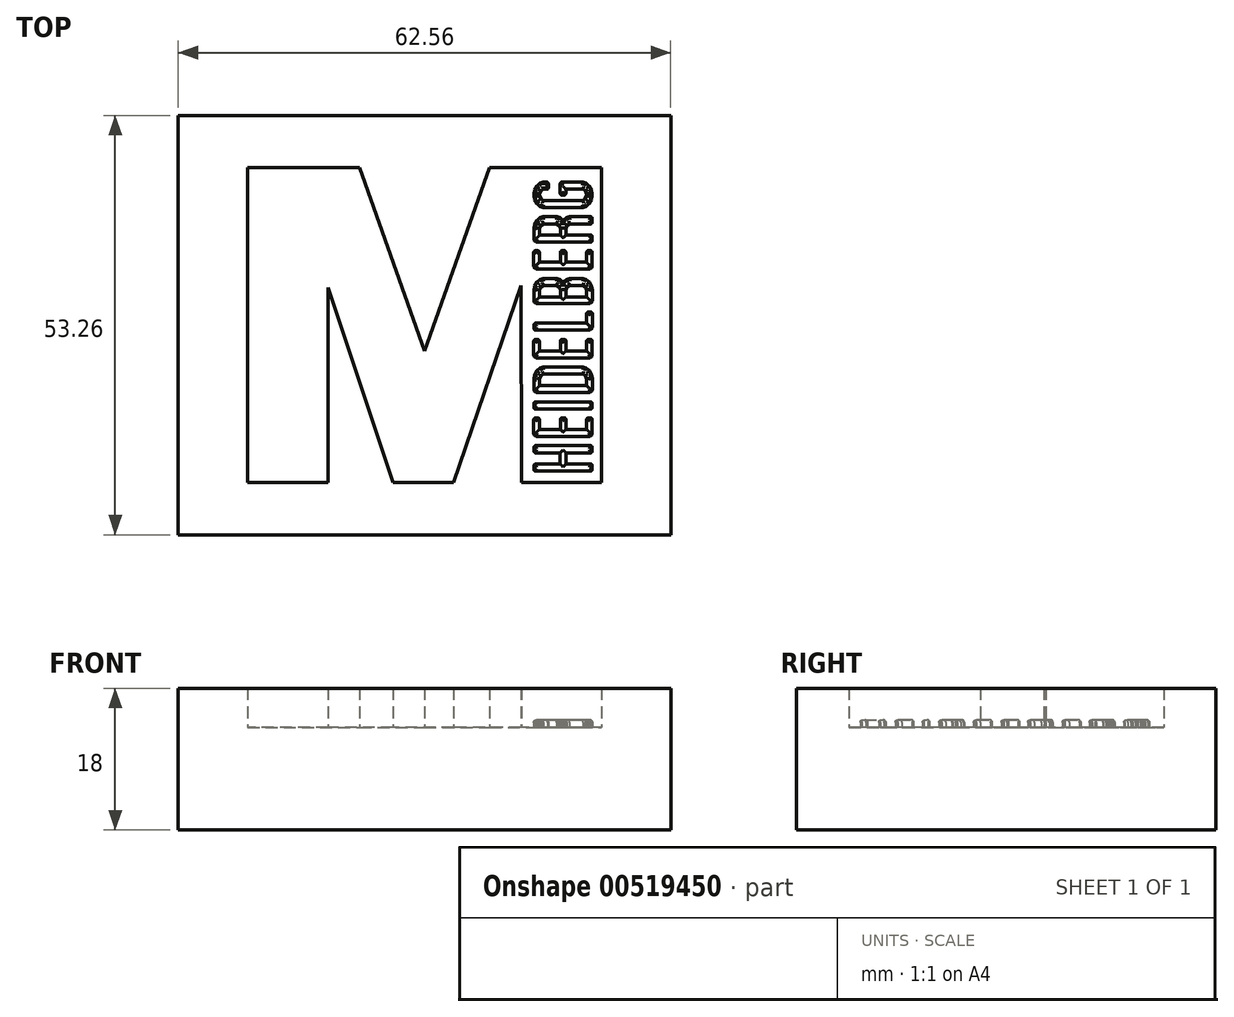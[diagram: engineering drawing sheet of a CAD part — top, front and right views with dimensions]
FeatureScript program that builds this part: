
annotation { "Feature Type Name" : "Feature", "Feature Type Description" : "" }
export const myFeature = defineFeature(function(context is Context, id is Id, definition is map)
    precondition{}
    {
        {
            var Q0;
            Q0=qCreatedBy(makeId("Top.planeOp"),FACE);
            var sketch = newSketch(context, id + "F0", { "sketchPlane" : qUnion([Q0])});
            skLineSegment(sketch, "E0", {"start": v(-22.46, 20) * mm, "end": v(-8.25, 20) * mm});
            skLineSegment(sketch, "E1", {"start": v(-8.25, 20) * mm, "end": v(0, -3.3) * mm});
            skLineSegment(sketch, "E2", {"start": v(0, -3.3) * mm, "end": v(8.3, 20) * mm});
            skLineSegment(sketch, "E3", {"start": v(8.3, 20) * mm, "end": v(22.46, 20) * mm});
            skLineSegment(sketch, "E4", {"start": v(22.46, 20) * mm, "end": v(22.46, -19.99) * mm});
            skLineSegment(sketch, "E5", {"start": v(22.46, -19.99) * mm, "end": v(12.3, -19.99) * mm});
            skLineSegment(sketch, "E6", {"start": v(12.3, -19.99) * mm, "end": v(12.26, 5.06) * mm});
            skLineSegment(sketch, "E7", {"start": v(12.26, 5.06) * mm, "end": v(3.69, -19.99) * mm});
            skLineSegment(sketch, "E8", {"start": v(3.69, -19.99) * mm, "end": v(-4.01, -19.99) * mm});
            skLineSegment(sketch, "E9", {"start": v(-4.01, -19.99) * mm, "end": v(-12.26, 4.79) * mm});
            skLineSegment(sketch, "E10", {"start": v(-12.26, 4.79) * mm, "end": v(-12.26, -20) * mm});
            skLineSegment(sketch, "E11", {"start": v(-12.26, -20) * mm, "end": v(-22.46, -20) * mm});
            skLineSegment(sketch, "E12", {"start": v(-22.46, -20) * mm, "end": v(-22.46, 20) * mm});
            skLineSegment(sketch, "E13", {"start": v(14.09, -15.3) * mm, "end": v(21.13, -15.3) * mm});
            skLineSegment(sketch, "E14", {"start": v(21.13, -15.3) * mm, "end": v(21.16, -15.3) * mm});
            skLineSegment(sketch, "E15", {"start": v(21.16, -15.3) * mm, "end": v(21.25, -15.37) * mm});
            skLineSegment(sketch, "E16", {"start": v(21.25, -15.37) * mm, "end": v(21.3, -15.5) * mm});
            skLineSegment(sketch, "E17", {"start": v(21.3, -15.5) * mm, "end": v(21.3, -15.54) * mm});
            skLineSegment(sketch, "E18", {"start": v(21.3, -15.54) * mm, "end": v(21.3, -15.98) * mm});
            skLineSegment(sketch, "E19", {"start": v(21.3, -15.98) * mm, "end": v(21.3, -16.02) * mm});
            skLineSegment(sketch, "E20", {"start": v(21.3, -16.02) * mm, "end": v(21.25, -16.14) * mm});
            skLineSegment(sketch, "E21", {"start": v(21.25, -16.14) * mm, "end": v(21.16, -16.2) * mm});
            skLineSegment(sketch, "E22", {"start": v(21.16, -16.2) * mm, "end": v(21.13, -16.2) * mm});
            skLineSegment(sketch, "E23", {"start": v(21.13, -16.2) * mm, "end": v(17.97, -16.2) * mm});
            skLineSegment(sketch, "E24", {"start": v(17.97, -16.2) * mm, "end": v(17.97, -17.65) * mm});
            skLineSegment(sketch, "E25", {"start": v(17.97, -17.65) * mm, "end": v(21.13, -17.65) * mm});
            skLineSegment(sketch, "E26", {"start": v(21.13, -17.65) * mm, "end": v(21.16, -17.65) * mm});
            skLineSegment(sketch, "E27", {"start": v(21.16, -17.65) * mm, "end": v(21.25, -17.71) * mm});
            skLineSegment(sketch, "E28", {"start": v(21.25, -17.71) * mm, "end": v(21.3, -17.84) * mm});
            skLineSegment(sketch, "E29", {"start": v(21.3, -17.84) * mm, "end": v(21.3, -17.88) * mm});
            skLineSegment(sketch, "E30", {"start": v(21.3, -17.88) * mm, "end": v(21.3, -18.32) * mm});
            skLineSegment(sketch, "E31", {"start": v(21.3, -18.32) * mm, "end": v(21.3, -18.36) * mm});
            skLineSegment(sketch, "E32", {"start": v(21.3, -18.36) * mm, "end": v(21.25, -18.49) * mm});
            skLineSegment(sketch, "E33", {"start": v(21.25, -18.49) * mm, "end": v(21.16, -18.55) * mm});
            skLineSegment(sketch, "E34", {"start": v(21.16, -18.55) * mm, "end": v(21.13, -18.55) * mm});
            skLineSegment(sketch, "E35", {"start": v(21.13, -18.55) * mm, "end": v(14.07, -18.55) * mm});
            skLineSegment(sketch, "E36", {"start": v(14.07, -18.55) * mm, "end": v(14.04, -18.55) * mm});
            skLineSegment(sketch, "E37", {"start": v(14.04, -18.55) * mm, "end": v(13.95, -18.49) * mm});
            skLineSegment(sketch, "E38", {"start": v(13.95, -18.49) * mm, "end": v(13.9, -18.36) * mm});
            skLineSegment(sketch, "E39", {"start": v(13.9, -18.36) * mm, "end": v(13.9, -18.32) * mm});
            skLineSegment(sketch, "E40", {"start": v(13.9, -18.32) * mm, "end": v(13.9, -17.88) * mm});
            skLineSegment(sketch, "E41", {"start": v(13.9, -17.88) * mm, "end": v(13.9, -17.84) * mm});
            skLineSegment(sketch, "E42", {"start": v(13.9, -17.84) * mm, "end": v(13.95, -17.71) * mm});
            skLineSegment(sketch, "E43", {"start": v(13.95, -17.71) * mm, "end": v(14.04, -17.65) * mm});
            skLineSegment(sketch, "E44", {"start": v(14.04, -17.65) * mm, "end": v(14.07, -17.65) * mm});
            skLineSegment(sketch, "E45", {"start": v(14.07, -17.65) * mm, "end": v(17.24, -17.65) * mm});
            skLineSegment(sketch, "E46", {"start": v(17.24, -17.65) * mm, "end": v(17.24, -16.2) * mm});
            skLineSegment(sketch, "E47", {"start": v(17.24, -16.2) * mm, "end": v(14.07, -16.2) * mm});
            skLineSegment(sketch, "E48", {"start": v(14.07, -16.2) * mm, "end": v(14.04, -16.2) * mm});
            skLineSegment(sketch, "E49", {"start": v(14.04, -16.2) * mm, "end": v(13.95, -16.14) * mm});
            skLineSegment(sketch, "E50", {"start": v(13.95, -16.14) * mm, "end": v(13.9, -16.02) * mm});
            skLineSegment(sketch, "E51", {"start": v(13.9, -16.02) * mm, "end": v(13.9, -15.98) * mm});
            skLineSegment(sketch, "E52", {"start": v(13.9, -15.98) * mm, "end": v(13.9, -15.54) * mm});
            skLineSegment(sketch, "E53", {"start": v(13.9, -15.54) * mm, "end": v(13.9, -15.5) * mm});
            skLineSegment(sketch, "E54", {"start": v(13.9, -15.5) * mm, "end": v(14.04, -15.3) * mm});
            skLineSegment(sketch, "E55", {"start": v(14.04, -15.3) * mm, "end": v(14.09, -15.3) * mm});
            skLineSegment(sketch, "E56", {"start": v(14.63, -13.23) * mm, "end": v(17.26, -13.23) * mm});
            skLineSegment(sketch, "E57", {"start": v(17.26, -13.23) * mm, "end": v(17.26, -12) * mm});
            skLineSegment(sketch, "E58", {"start": v(17.26, -12) * mm, "end": v(17.26, -11.96) * mm});
            skLineSegment(sketch, "E59", {"start": v(17.26, -11.96) * mm, "end": v(17.3, -11.84) * mm});
            skLineSegment(sketch, "E60", {"start": v(17.3, -11.84) * mm, "end": v(17.4, -11.78) * mm});
            skLineSegment(sketch, "E61", {"start": v(17.4, -11.78) * mm, "end": v(17.43, -11.78) * mm});
            skLineSegment(sketch, "E62", {"start": v(17.43, -11.78) * mm, "end": v(17.8, -11.78) * mm});
            skLineSegment(sketch, "E63", {"start": v(17.8, -11.78) * mm, "end": v(17.82, -11.78) * mm});
            skLineSegment(sketch, "E64", {"start": v(17.82, -11.78) * mm, "end": v(17.91, -11.84) * mm});
            skLineSegment(sketch, "E65", {"start": v(17.91, -11.84) * mm, "end": v(17.97, -11.96) * mm});
            skLineSegment(sketch, "E66", {"start": v(17.97, -11.96) * mm, "end": v(17.97, -12) * mm});
            skLineSegment(sketch, "E67", {"start": v(17.97, -12) * mm, "end": v(17.97, -13.23) * mm});
            skLineSegment(sketch, "E68", {"start": v(17.97, -13.23) * mm, "end": v(20.6, -13.23) * mm});
            skLineSegment(sketch, "E69", {"start": v(20.6, -13.23) * mm, "end": v(20.6, -12) * mm});
            skLineSegment(sketch, "E70", {"start": v(20.6, -12) * mm, "end": v(20.6, -11.96) * mm});
            skLineSegment(sketch, "E71", {"start": v(20.6, -11.96) * mm, "end": v(20.65, -11.84) * mm});
            skLineSegment(sketch, "E72", {"start": v(20.65, -11.84) * mm, "end": v(20.74, -11.78) * mm});
            skLineSegment(sketch, "E73", {"start": v(20.74, -11.78) * mm, "end": v(20.77, -11.78) * mm});
            skLineSegment(sketch, "E74", {"start": v(20.77, -11.78) * mm, "end": v(21.13, -11.78) * mm});
            skLineSegment(sketch, "E75", {"start": v(21.13, -11.78) * mm, "end": v(21.16, -11.78) * mm});
            skLineSegment(sketch, "E76", {"start": v(21.16, -11.78) * mm, "end": v(21.25, -11.84) * mm});
            skLineSegment(sketch, "E77", {"start": v(21.25, -11.84) * mm, "end": v(21.3, -11.96) * mm});
            skLineSegment(sketch, "E78", {"start": v(21.3, -11.96) * mm, "end": v(21.3, -12) * mm});
            skLineSegment(sketch, "E79", {"start": v(21.3, -12) * mm, "end": v(21.3, -13.67) * mm});
            skLineSegment(sketch, "E80", {"start": v(21.3, -13.67) * mm, "end": v(21.3, -13.75) * mm});
            skLineSegment(sketch, "E81", {"start": v(21.3, -13.75) * mm, "end": v(21.2, -13.99) * mm});
            skLineSegment(sketch, "E82", {"start": v(21.2, -13.99) * mm, "end": v(21, -14.12) * mm});
            skLineSegment(sketch, "E83", {"start": v(21, -14.12) * mm, "end": v(20.94, -14.12) * mm});
            skLineSegment(sketch, "E84", {"start": v(20.94, -14.12) * mm, "end": v(14.24, -14.12) * mm});
            skLineSegment(sketch, "E85", {"start": v(14.24, -14.12) * mm, "end": v(14.18, -14.12) * mm});
            skLineSegment(sketch, "E86", {"start": v(14.18, -14.12) * mm, "end": v(13.99, -13.99) * mm});
            skLineSegment(sketch, "E87", {"start": v(13.99, -13.99) * mm, "end": v(13.88, -13.75) * mm});
            skLineSegment(sketch, "E88", {"start": v(13.88, -13.75) * mm, "end": v(13.88, -13.67) * mm});
            skLineSegment(sketch, "E89", {"start": v(13.88, -13.67) * mm, "end": v(13.88, -12) * mm});
            skLineSegment(sketch, "E90", {"start": v(13.88, -12) * mm, "end": v(13.88, -11.96) * mm});
            skLineSegment(sketch, "E91", {"start": v(13.88, -11.96) * mm, "end": v(13.93, -11.84) * mm});
            skLineSegment(sketch, "E92", {"start": v(13.93, -11.84) * mm, "end": v(14.02, -11.78) * mm});
            skLineSegment(sketch, "E93", {"start": v(14.02, -11.78) * mm, "end": v(14.05, -11.78) * mm});
            skLineSegment(sketch, "E94", {"start": v(14.05, -11.78) * mm, "end": v(14.41, -11.78) * mm});
            skLineSegment(sketch, "E95", {"start": v(14.41, -11.78) * mm, "end": v(14.44, -11.78) * mm});
            skLineSegment(sketch, "E96", {"start": v(14.44, -11.78) * mm, "end": v(14.54, -11.84) * mm});
            skLineSegment(sketch, "E97", {"start": v(14.54, -11.84) * mm, "end": v(14.59, -11.96) * mm});
            skLineSegment(sketch, "E98", {"start": v(14.59, -11.96) * mm, "end": v(14.59, -12) * mm});
            skLineSegment(sketch, "E99", {"start": v(14.59, -12) * mm, "end": v(14.59, -13.23) * mm});
            skLineSegment(sketch, "E100", {"start": v(14.59, -13.23) * mm, "end": v(14.63, -13.23) * mm});
            skLineSegment(sketch, "E101", {"start": v(21.13, -9.74) * mm, "end": v(21.16, -9.74) * mm});
            skLineSegment(sketch, "E102", {"start": v(21.16, -9.74) * mm, "end": v(21.25, -9.8) * mm});
            skLineSegment(sketch, "E103", {"start": v(21.25, -9.8) * mm, "end": v(21.3, -9.93) * mm});
            skLineSegment(sketch, "E104", {"start": v(21.3, -9.93) * mm, "end": v(21.3, -9.97) * mm});
            skLineSegment(sketch, "E105", {"start": v(21.3, -9.97) * mm, "end": v(21.3, -10.41) * mm});
            skLineSegment(sketch, "E106", {"start": v(21.3, -10.41) * mm, "end": v(21.3, -10.45) * mm});
            skLineSegment(sketch, "E107", {"start": v(21.3, -10.45) * mm, "end": v(21.25, -10.58) * mm});
            skLineSegment(sketch, "E108", {"start": v(21.25, -10.58) * mm, "end": v(21.16, -10.64) * mm});
            skLineSegment(sketch, "E109", {"start": v(21.16, -10.64) * mm, "end": v(21.13, -10.64) * mm});
            skLineSegment(sketch, "E110", {"start": v(21.13, -10.64) * mm, "end": v(14.07, -10.64) * mm});
            skLineSegment(sketch, "E111", {"start": v(14.07, -10.64) * mm, "end": v(14.04, -10.64) * mm});
            skLineSegment(sketch, "E112", {"start": v(14.04, -10.64) * mm, "end": v(13.95, -10.58) * mm});
            skLineSegment(sketch, "E113", {"start": v(13.95, -10.58) * mm, "end": v(13.9, -10.45) * mm});
            skLineSegment(sketch, "E114", {"start": v(13.9, -10.45) * mm, "end": v(13.9, -10.41) * mm});
            skLineSegment(sketch, "E115", {"start": v(13.9, -10.41) * mm, "end": v(13.9, -9.97) * mm});
            skLineSegment(sketch, "E116", {"start": v(13.9, -9.97) * mm, "end": v(13.9, -9.93) * mm});
            skLineSegment(sketch, "E117", {"start": v(13.9, -9.93) * mm, "end": v(13.95, -9.8) * mm});
            skLineSegment(sketch, "E118", {"start": v(13.95, -9.8) * mm, "end": v(14.04, -9.74) * mm});
            skLineSegment(sketch, "E119", {"start": v(14.04, -9.74) * mm, "end": v(14.07, -9.74) * mm});
            skLineSegment(sketch, "E120", {"start": v(14.07, -9.74) * mm, "end": v(21.13, -9.74) * mm});
            skLineSegment(sketch, "E121", {"start": v(15.2, -5.33) * mm, "end": v(20.04, -5.33) * mm});
            skLineSegment(sketch, "E122", {"start": v(20.04, -5.33) * mm, "end": v(20.16, -5.33) * mm});
            skLineSegment(sketch, "E123", {"start": v(20.16, -5.33) * mm, "end": v(20.54, -5.45) * mm});
            skLineSegment(sketch, "E124", {"start": v(20.54, -5.45) * mm, "end": v(20.95, -5.8) * mm});
            skLineSegment(sketch, "E125", {"start": v(20.95, -5.8) * mm, "end": v(21.22, -6.3) * mm});
            skLineSegment(sketch, "E126", {"start": v(21.22, -6.3) * mm, "end": v(21.32, -6.78) * mm});
            skLineSegment(sketch, "E127", {"start": v(21.32, -6.78) * mm, "end": v(21.32, -6.94) * mm});
            skLineSegment(sketch, "E128", {"start": v(21.32, -6.94) * mm, "end": v(21.32, -8.1) * mm});
            skLineSegment(sketch, "E129", {"start": v(21.32, -8.1) * mm, "end": v(21.32, -8.18) * mm});
            skLineSegment(sketch, "E130", {"start": v(21.32, -8.18) * mm, "end": v(21.22, -8.42) * mm});
            skLineSegment(sketch, "E131", {"start": v(21.22, -8.42) * mm, "end": v(21.02, -8.55) * mm});
            skLineSegment(sketch, "E132", {"start": v(21.02, -8.55) * mm, "end": v(20.96, -8.55) * mm});
            skLineSegment(sketch, "E133", {"start": v(20.96, -8.55) * mm, "end": v(14.26, -8.55) * mm});
            skLineSegment(sketch, "E134", {"start": v(14.26, -8.55) * mm, "end": v(14.2, -8.55) * mm});
            skLineSegment(sketch, "E135", {"start": v(14.2, -8.55) * mm, "end": v(14, -8.42) * mm});
            skLineSegment(sketch, "E136", {"start": v(14, -8.42) * mm, "end": v(13.9, -8.18) * mm});
            skLineSegment(sketch, "E137", {"start": v(13.9, -8.18) * mm, "end": v(13.9, -8.1) * mm});
            skLineSegment(sketch, "E138", {"start": v(13.9, -8.1) * mm, "end": v(13.9, -6.94) * mm});
            skLineSegment(sketch, "E139", {"start": v(13.9, -6.94) * mm, "end": v(13.9, -6.78) * mm});
            skLineSegment(sketch, "E140", {"start": v(13.9, -6.78) * mm, "end": v(14, -6.3) * mm});
            skLineSegment(sketch, "E141", {"start": v(14, -6.3) * mm, "end": v(14.29, -5.8) * mm});
            skLineSegment(sketch, "E142", {"start": v(14.29, -5.8) * mm, "end": v(14.7, -5.45) * mm});
            skLineSegment(sketch, "E143", {"start": v(14.7, -5.45) * mm, "end": v(15.08, -5.33) * mm});
            skLineSegment(sketch, "E144", {"start": v(15.08, -5.33) * mm, "end": v(15.2, -5.33) * mm});
            skLineSegment(sketch, "E145", {"start": v(15.2, -6.23) * mm, "end": v(15.1, -6.23) * mm});
            skLineSegment(sketch, "E146", {"start": v(15.1, -6.23) * mm, "end": v(14.8, -6.44) * mm});
            skLineSegment(sketch, "E147", {"start": v(14.8, -6.44) * mm, "end": v(14.63, -6.81) * mm});
            skLineSegment(sketch, "E148", {"start": v(14.63, -6.81) * mm, "end": v(14.63, -6.94) * mm});
            skLineSegment(sketch, "E149", {"start": v(14.63, -6.94) * mm, "end": v(14.63, -7.67) * mm});
            skLineSegment(sketch, "E150", {"start": v(14.63, -7.67) * mm, "end": v(20.6, -7.67) * mm});
            skLineSegment(sketch, "E151", {"start": v(20.6, -7.67) * mm, "end": v(20.6, -6.94) * mm});
            skLineSegment(sketch, "E152", {"start": v(20.6, -6.94) * mm, "end": v(20.6, -6.81) * mm});
            skLineSegment(sketch, "E153", {"start": v(20.6, -6.81) * mm, "end": v(20.43, -6.44) * mm});
            skLineSegment(sketch, "E154", {"start": v(20.43, -6.44) * mm, "end": v(20.12, -6.23) * mm});
            skLineSegment(sketch, "E155", {"start": v(20.12, -6.23) * mm, "end": v(20.02, -6.23) * mm});
            skLineSegment(sketch, "E156", {"start": v(20.02, -6.23) * mm, "end": v(15.2, -6.23) * mm});
            skLineSegment(sketch, "E157", {"start": v(14.63, -3.27) * mm, "end": v(17.26, -3.27) * mm});
            skLineSegment(sketch, "E158", {"start": v(17.26, -3.27) * mm, "end": v(17.26, -2.04) * mm});
            skLineSegment(sketch, "E159", {"start": v(17.26, -2.04) * mm, "end": v(17.26, -2) * mm});
            skLineSegment(sketch, "E160", {"start": v(17.26, -2) * mm, "end": v(17.3, -1.88) * mm});
            skLineSegment(sketch, "E161", {"start": v(17.3, -1.88) * mm, "end": v(17.4, -1.81) * mm});
            skLineSegment(sketch, "E162", {"start": v(17.4, -1.81) * mm, "end": v(17.43, -1.81) * mm});
            skLineSegment(sketch, "E163", {"start": v(17.43, -1.81) * mm, "end": v(17.8, -1.81) * mm});
            skLineSegment(sketch, "E164", {"start": v(17.8, -1.81) * mm, "end": v(17.82, -1.81) * mm});
            skLineSegment(sketch, "E165", {"start": v(17.82, -1.81) * mm, "end": v(17.91, -1.88) * mm});
            skLineSegment(sketch, "E166", {"start": v(17.91, -1.88) * mm, "end": v(17.97, -2) * mm});
            skLineSegment(sketch, "E167", {"start": v(17.97, -2) * mm, "end": v(17.97, -2.04) * mm});
            skLineSegment(sketch, "E168", {"start": v(17.97, -2.04) * mm, "end": v(17.97, -3.27) * mm});
            skLineSegment(sketch, "E169", {"start": v(17.97, -3.27) * mm, "end": v(20.6, -3.27) * mm});
            skLineSegment(sketch, "E170", {"start": v(20.6, -3.27) * mm, "end": v(20.6, -2.04) * mm});
            skLineSegment(sketch, "E171", {"start": v(20.6, -2.04) * mm, "end": v(20.6, -2) * mm});
            skLineSegment(sketch, "E172", {"start": v(20.6, -2) * mm, "end": v(20.65, -1.88) * mm});
            skLineSegment(sketch, "E173", {"start": v(20.65, -1.88) * mm, "end": v(20.74, -1.81) * mm});
            skLineSegment(sketch, "E174", {"start": v(20.74, -1.81) * mm, "end": v(20.77, -1.81) * mm});
            skLineSegment(sketch, "E175", {"start": v(20.77, -1.81) * mm, "end": v(21.13, -1.81) * mm});
            skLineSegment(sketch, "E176", {"start": v(21.13, -1.81) * mm, "end": v(21.16, -1.81) * mm});
            skLineSegment(sketch, "E177", {"start": v(21.16, -1.81) * mm, "end": v(21.25, -1.88) * mm});
            skLineSegment(sketch, "E178", {"start": v(21.25, -1.88) * mm, "end": v(21.3, -2) * mm});
            skLineSegment(sketch, "E179", {"start": v(21.3, -2) * mm, "end": v(21.3, -2.04) * mm});
            skLineSegment(sketch, "E180", {"start": v(21.3, -2.04) * mm, "end": v(21.3, -3.71) * mm});
            skLineSegment(sketch, "E181", {"start": v(21.3, -3.71) * mm, "end": v(21.3, -3.8) * mm});
            skLineSegment(sketch, "E182", {"start": v(21.3, -3.8) * mm, "end": v(21.2, -4.03) * mm});
            skLineSegment(sketch, "E183", {"start": v(21.2, -4.03) * mm, "end": v(21, -4.16) * mm});
            skLineSegment(sketch, "E184", {"start": v(21, -4.16) * mm, "end": v(20.94, -4.16) * mm});
            skLineSegment(sketch, "E185", {"start": v(20.94, -4.16) * mm, "end": v(14.24, -4.16) * mm});
            skLineSegment(sketch, "E186", {"start": v(14.24, -4.16) * mm, "end": v(14.18, -4.16) * mm});
            skLineSegment(sketch, "E187", {"start": v(14.18, -4.16) * mm, "end": v(13.99, -4.03) * mm});
            skLineSegment(sketch, "E188", {"start": v(13.99, -4.03) * mm, "end": v(13.88, -3.8) * mm});
            skLineSegment(sketch, "E189", {"start": v(13.88, -3.8) * mm, "end": v(13.88, -3.71) * mm});
            skLineSegment(sketch, "E190", {"start": v(13.88, -3.71) * mm, "end": v(13.88, -2.04) * mm});
            skLineSegment(sketch, "E191", {"start": v(13.88, -2.04) * mm, "end": v(13.88, -2) * mm});
            skLineSegment(sketch, "E192", {"start": v(13.88, -2) * mm, "end": v(13.93, -1.88) * mm});
            skLineSegment(sketch, "E193", {"start": v(13.93, -1.88) * mm, "end": v(14.02, -1.81) * mm});
            skLineSegment(sketch, "E194", {"start": v(14.02, -1.81) * mm, "end": v(14.05, -1.81) * mm});
            skLineSegment(sketch, "E195", {"start": v(14.05, -1.81) * mm, "end": v(14.41, -1.81) * mm});
            skLineSegment(sketch, "E196", {"start": v(14.41, -1.81) * mm, "end": v(14.44, -1.81) * mm});
            skLineSegment(sketch, "E197", {"start": v(14.44, -1.81) * mm, "end": v(14.54, -1.88) * mm});
            skLineSegment(sketch, "E198", {"start": v(14.54, -1.88) * mm, "end": v(14.59, -2) * mm});
            skLineSegment(sketch, "E199", {"start": v(14.59, -2) * mm, "end": v(14.59, -2.04) * mm});
            skLineSegment(sketch, "E200", {"start": v(14.59, -2.04) * mm, "end": v(14.59, -3.27) * mm});
            skLineSegment(sketch, "E201", {"start": v(14.59, -3.27) * mm, "end": v(14.63, -3.27) * mm});
            skLineSegment(sketch, "E202", {"start": v(20.79, 1.68) * mm, "end": v(21.15, 1.68) * mm});
            skLineSegment(sketch, "E203", {"start": v(21.15, 1.68) * mm, "end": v(21.18, 1.68) * mm});
            skLineSegment(sketch, "E204", {"start": v(21.18, 1.68) * mm, "end": v(21.27, 1.62) * mm});
            skLineSegment(sketch, "E205", {"start": v(21.27, 1.62) * mm, "end": v(21.32, 1.5) * mm});
            skLineSegment(sketch, "E206", {"start": v(21.32, 1.5) * mm, "end": v(21.32, 1.45) * mm});
            skLineSegment(sketch, "E207", {"start": v(21.32, 1.45) * mm, "end": v(21.32, -0.2) * mm});
            skLineSegment(sketch, "E208", {"start": v(21.32, -0.2) * mm, "end": v(21.32, -0.28) * mm});
            skLineSegment(sketch, "E209", {"start": v(21.32, -0.28) * mm, "end": v(21.22, -0.51) * mm});
            skLineSegment(sketch, "E210", {"start": v(21.22, -0.51) * mm, "end": v(21.02, -0.64) * mm});
            skLineSegment(sketch, "E211", {"start": v(21.02, -0.64) * mm, "end": v(20.96, -0.64) * mm});
            skLineSegment(sketch, "E212", {"start": v(20.96, -0.64) * mm, "end": v(14.09, -0.64) * mm});
            skLineSegment(sketch, "E213", {"start": v(14.09, -0.64) * mm, "end": v(14.06, -0.64) * mm});
            skLineSegment(sketch, "E214", {"start": v(14.06, -0.64) * mm, "end": v(13.97, -0.58) * mm});
            skLineSegment(sketch, "E215", {"start": v(13.97, -0.58) * mm, "end": v(13.92, -0.45) * mm});
            skLineSegment(sketch, "E216", {"start": v(13.92, -0.45) * mm, "end": v(13.92, -0.41) * mm});
            skLineSegment(sketch, "E217", {"start": v(13.92, -0.41) * mm, "end": v(13.92, 0.03) * mm});
            skLineSegment(sketch, "E218", {"start": v(13.92, 0.03) * mm, "end": v(13.92, 0.07) * mm});
            skLineSegment(sketch, "E219", {"start": v(13.92, 0.07) * mm, "end": v(13.97, 0.19) * mm});
            skLineSegment(sketch, "E220", {"start": v(13.97, 0.19) * mm, "end": v(14.06, 0.26) * mm});
            skLineSegment(sketch, "E221", {"start": v(14.06, 0.26) * mm, "end": v(14.09, 0.26) * mm});
            skLineSegment(sketch, "E222", {"start": v(14.09, 0.26) * mm, "end": v(20.6, 0.26) * mm});
            skLineSegment(sketch, "E223", {"start": v(20.6, 0.26) * mm, "end": v(20.6, 1.47) * mm});
            skLineSegment(sketch, "E224", {"start": v(20.6, 1.47) * mm, "end": v(20.6, 1.5) * mm});
            skLineSegment(sketch, "E225", {"start": v(20.6, 1.5) * mm, "end": v(20.65, 1.62) * mm});
            skLineSegment(sketch, "E226", {"start": v(20.65, 1.62) * mm, "end": v(20.75, 1.68) * mm});
            skLineSegment(sketch, "E227", {"start": v(20.75, 1.68) * mm, "end": v(20.79, 1.68) * mm});
            skLineSegment(sketch, "E228", {"start": v(16.68, 5.94) * mm, "end": v(16.8, 5.94) * mm});
            skLineSegment(sketch, "E229", {"start": v(16.8, 5.94) * mm, "end": v(17.2, 5.8) * mm});
            skLineSegment(sketch, "E230", {"start": v(17.2, 5.8) * mm, "end": v(17.56, 5.52) * mm});
            skLineSegment(sketch, "E231", {"start": v(17.56, 5.52) * mm, "end": v(17.62, 5.44) * mm});
            skLineSegment(sketch, "E232", {"start": v(17.62, 5.44) * mm, "end": v(17.68, 5.52) * mm});
            skLineSegment(sketch, "E233", {"start": v(17.68, 5.52) * mm, "end": v(18.03, 5.8) * mm});
            skLineSegment(sketch, "E234", {"start": v(18.03, 5.8) * mm, "end": v(18.41, 5.94) * mm});
            skLineSegment(sketch, "E235", {"start": v(18.41, 5.94) * mm, "end": v(18.54, 5.94) * mm});
            skLineSegment(sketch, "E236", {"start": v(18.54, 5.94) * mm, "end": v(20.04, 5.94) * mm});
            skLineSegment(sketch, "E237", {"start": v(20.04, 5.94) * mm, "end": v(20.16, 5.94) * mm});
            skLineSegment(sketch, "E238", {"start": v(20.16, 5.94) * mm, "end": v(20.54, 5.81) * mm});
            skLineSegment(sketch, "E239", {"start": v(20.54, 5.81) * mm, "end": v(20.95, 5.47) * mm});
            skLineSegment(sketch, "E240", {"start": v(20.95, 5.47) * mm, "end": v(21.22, 4.95) * mm});
            skLineSegment(sketch, "E241", {"start": v(21.22, 4.95) * mm, "end": v(21.32, 4.48) * mm});
            skLineSegment(sketch, "E242", {"start": v(21.32, 4.48) * mm, "end": v(21.32, 4.33) * mm});
            skLineSegment(sketch, "E243", {"start": v(21.32, 4.33) * mm, "end": v(21.32, 3.16) * mm});
            skLineSegment(sketch, "E244", {"start": v(21.32, 3.16) * mm, "end": v(21.32, 3.08) * mm});
            skLineSegment(sketch, "E245", {"start": v(21.32, 3.08) * mm, "end": v(21.22, 2.85) * mm});
            skLineSegment(sketch, "E246", {"start": v(21.22, 2.85) * mm, "end": v(21.02, 2.72) * mm});
            skLineSegment(sketch, "E247", {"start": v(21.02, 2.72) * mm, "end": v(20.96, 2.72) * mm});
            skLineSegment(sketch, "E248", {"start": v(20.96, 2.72) * mm, "end": v(14.26, 2.72) * mm});
            skLineSegment(sketch, "E249", {"start": v(14.26, 2.72) * mm, "end": v(14.2, 2.72) * mm});
            skLineSegment(sketch, "E250", {"start": v(14.2, 2.72) * mm, "end": v(14, 2.85) * mm});
            skLineSegment(sketch, "E251", {"start": v(14, 2.85) * mm, "end": v(13.9, 3.08) * mm});
            skLineSegment(sketch, "E252", {"start": v(13.9, 3.08) * mm, "end": v(13.9, 3.16) * mm});
            skLineSegment(sketch, "E253", {"start": v(13.9, 3.16) * mm, "end": v(13.9, 4.33) * mm});
            skLineSegment(sketch, "E254", {"start": v(13.9, 4.33) * mm, "end": v(13.9, 4.48) * mm});
            skLineSegment(sketch, "E255", {"start": v(13.9, 4.48) * mm, "end": v(14, 4.95) * mm});
            skLineSegment(sketch, "E256", {"start": v(14, 4.95) * mm, "end": v(14.27, 5.47) * mm});
            skLineSegment(sketch, "E257", {"start": v(14.27, 5.47) * mm, "end": v(14.68, 5.81) * mm});
            skLineSegment(sketch, "E258", {"start": v(14.68, 5.81) * mm, "end": v(15.06, 5.94) * mm});
            skLineSegment(sketch, "E259", {"start": v(15.06, 5.94) * mm, "end": v(15.18, 5.94) * mm});
            skLineSegment(sketch, "E260", {"start": v(15.18, 5.94) * mm, "end": v(16.68, 5.94) * mm});
            skLineSegment(sketch, "E261", {"start": v(15.2, 5.04) * mm, "end": v(15.1, 5.04) * mm});
            skLineSegment(sketch, "E262", {"start": v(15.1, 5.04) * mm, "end": v(14.8, 4.83) * mm});
            skLineSegment(sketch, "E263", {"start": v(14.8, 4.83) * mm, "end": v(14.63, 4.45) * mm});
            skLineSegment(sketch, "E264", {"start": v(14.63, 4.45) * mm, "end": v(14.63, 4.33) * mm});
            skLineSegment(sketch, "E265", {"start": v(14.63, 4.33) * mm, "end": v(14.63, 3.6) * mm});
            skLineSegment(sketch, "E266", {"start": v(14.63, 3.6) * mm, "end": v(17.26, 3.6) * mm});
            skLineSegment(sketch, "E267", {"start": v(17.26, 3.6) * mm, "end": v(17.26, 4.33) * mm});
            skLineSegment(sketch, "E268", {"start": v(17.26, 4.33) * mm, "end": v(17.26, 4.45) * mm});
            skLineSegment(sketch, "E269", {"start": v(17.26, 4.45) * mm, "end": v(17.09, 4.83) * mm});
            skLineSegment(sketch, "E270", {"start": v(17.09, 4.83) * mm, "end": v(16.78, 5.04) * mm});
            skLineSegment(sketch, "E271", {"start": v(16.78, 5.04) * mm, "end": v(16.68, 5.04) * mm});
            skLineSegment(sketch, "E272", {"start": v(16.68, 5.04) * mm, "end": v(15.2, 5.04) * mm});
            skLineSegment(sketch, "E273", {"start": v(17.97, 4.33) * mm, "end": v(17.97, 3.6) * mm});
            skLineSegment(sketch, "E274", {"start": v(17.97, 3.6) * mm, "end": v(20.6, 3.6) * mm});
            skLineSegment(sketch, "E275", {"start": v(20.6, 3.6) * mm, "end": v(20.6, 4.33) * mm});
            skLineSegment(sketch, "E276", {"start": v(20.6, 4.33) * mm, "end": v(20.6, 4.45) * mm});
            skLineSegment(sketch, "E277", {"start": v(20.6, 4.45) * mm, "end": v(20.43, 4.83) * mm});
            skLineSegment(sketch, "E278", {"start": v(20.43, 4.83) * mm, "end": v(20.12, 5.04) * mm});
            skLineSegment(sketch, "E279", {"start": v(20.12, 5.04) * mm, "end": v(20.02, 5.04) * mm});
            skLineSegment(sketch, "E280", {"start": v(20.02, 5.04) * mm, "end": v(18.52, 5.04) * mm});
            skLineSegment(sketch, "E281", {"start": v(18.52, 5.04) * mm, "end": v(18.42, 5.04) * mm});
            skLineSegment(sketch, "E282", {"start": v(18.42, 5.04) * mm, "end": v(18.13, 4.83) * mm});
            skLineSegment(sketch, "E283", {"start": v(18.13, 4.83) * mm, "end": v(17.97, 4.45) * mm});
            skLineSegment(sketch, "E284", {"start": v(17.97, 4.45) * mm, "end": v(17.97, 4.33) * mm});
            skLineSegment(sketch, "E285", {"start": v(14.63, 8) * mm, "end": v(17.26, 8) * mm});
            skLineSegment(sketch, "E286", {"start": v(17.26, 8) * mm, "end": v(17.26, 9.22) * mm});
            skLineSegment(sketch, "E287", {"start": v(17.26, 9.22) * mm, "end": v(17.26, 9.26) * mm});
            skLineSegment(sketch, "E288", {"start": v(17.26, 9.26) * mm, "end": v(17.3, 9.39) * mm});
            skLineSegment(sketch, "E289", {"start": v(17.3, 9.39) * mm, "end": v(17.4, 9.45) * mm});
            skLineSegment(sketch, "E290", {"start": v(17.4, 9.45) * mm, "end": v(17.43, 9.45) * mm});
            skLineSegment(sketch, "E291", {"start": v(17.43, 9.45) * mm, "end": v(17.8, 9.45) * mm});
            skLineSegment(sketch, "E292", {"start": v(17.8, 9.45) * mm, "end": v(17.82, 9.45) * mm});
            skLineSegment(sketch, "E293", {"start": v(17.82, 9.45) * mm, "end": v(17.91, 9.39) * mm});
            skLineSegment(sketch, "E294", {"start": v(17.91, 9.39) * mm, "end": v(17.97, 9.26) * mm});
            skLineSegment(sketch, "E295", {"start": v(17.97, 9.26) * mm, "end": v(17.97, 9.22) * mm});
            skLineSegment(sketch, "E296", {"start": v(17.97, 9.22) * mm, "end": v(17.97, 8) * mm});
            skLineSegment(sketch, "E297", {"start": v(17.97, 8) * mm, "end": v(20.6, 8) * mm});
            skLineSegment(sketch, "E298", {"start": v(20.6, 8) * mm, "end": v(20.6, 9.22) * mm});
            skLineSegment(sketch, "E299", {"start": v(20.6, 9.22) * mm, "end": v(20.6, 9.26) * mm});
            skLineSegment(sketch, "E300", {"start": v(20.6, 9.26) * mm, "end": v(20.65, 9.39) * mm});
            skLineSegment(sketch, "E301", {"start": v(20.65, 9.39) * mm, "end": v(20.74, 9.45) * mm});
            skLineSegment(sketch, "E302", {"start": v(20.74, 9.45) * mm, "end": v(20.77, 9.45) * mm});
            skLineSegment(sketch, "E303", {"start": v(20.77, 9.45) * mm, "end": v(21.13, 9.45) * mm});
            skLineSegment(sketch, "E304", {"start": v(21.13, 9.45) * mm, "end": v(21.16, 9.45) * mm});
            skLineSegment(sketch, "E305", {"start": v(21.16, 9.45) * mm, "end": v(21.25, 9.39) * mm});
            skLineSegment(sketch, "E306", {"start": v(21.25, 9.39) * mm, "end": v(21.3, 9.26) * mm});
            skLineSegment(sketch, "E307", {"start": v(21.3, 9.26) * mm, "end": v(21.3, 9.22) * mm});
            skLineSegment(sketch, "E308", {"start": v(21.3, 9.22) * mm, "end": v(21.3, 7.55) * mm});
            skLineSegment(sketch, "E309", {"start": v(21.3, 7.55) * mm, "end": v(21.3, 7.47) * mm});
            skLineSegment(sketch, "E310", {"start": v(21.3, 7.47) * mm, "end": v(21.2, 7.24) * mm});
            skLineSegment(sketch, "E311", {"start": v(21.2, 7.24) * mm, "end": v(21, 7.11) * mm});
            skLineSegment(sketch, "E312", {"start": v(21, 7.11) * mm, "end": v(20.94, 7.11) * mm});
            skLineSegment(sketch, "E313", {"start": v(20.94, 7.11) * mm, "end": v(14.24, 7.11) * mm});
            skLineSegment(sketch, "E314", {"start": v(14.24, 7.11) * mm, "end": v(14.18, 7.11) * mm});
            skLineSegment(sketch, "E315", {"start": v(14.18, 7.11) * mm, "end": v(13.99, 7.24) * mm});
            skLineSegment(sketch, "E316", {"start": v(13.99, 7.24) * mm, "end": v(13.88, 7.47) * mm});
            skLineSegment(sketch, "E317", {"start": v(13.88, 7.47) * mm, "end": v(13.88, 7.55) * mm});
            skLineSegment(sketch, "E318", {"start": v(13.88, 7.55) * mm, "end": v(13.88, 9.22) * mm});
            skLineSegment(sketch, "E319", {"start": v(13.88, 9.22) * mm, "end": v(13.88, 9.26) * mm});
            skLineSegment(sketch, "E320", {"start": v(13.88, 9.26) * mm, "end": v(13.93, 9.39) * mm});
            skLineSegment(sketch, "E321", {"start": v(13.93, 9.39) * mm, "end": v(14.02, 9.45) * mm});
            skLineSegment(sketch, "E322", {"start": v(14.02, 9.45) * mm, "end": v(14.05, 9.45) * mm});
            skLineSegment(sketch, "E323", {"start": v(14.05, 9.45) * mm, "end": v(14.41, 9.45) * mm});
            skLineSegment(sketch, "E324", {"start": v(14.41, 9.45) * mm, "end": v(14.44, 9.45) * mm});
            skLineSegment(sketch, "E325", {"start": v(14.44, 9.45) * mm, "end": v(14.54, 9.39) * mm});
            skLineSegment(sketch, "E326", {"start": v(14.54, 9.39) * mm, "end": v(14.59, 9.26) * mm});
            skLineSegment(sketch, "E327", {"start": v(14.59, 9.26) * mm, "end": v(14.59, 9.22) * mm});
            skLineSegment(sketch, "E328", {"start": v(14.59, 9.22) * mm, "end": v(14.59, 8) * mm});
            skLineSegment(sketch, "E329", {"start": v(14.59, 8) * mm, "end": v(14.63, 8) * mm});
            skLineSegment(sketch, "E330", {"start": v(16.68, 13.77) * mm, "end": v(16.8, 13.77) * mm});
            skLineSegment(sketch, "E331", {"start": v(16.8, 13.77) * mm, "end": v(17.2, 13.64) * mm});
            skLineSegment(sketch, "E332", {"start": v(17.2, 13.64) * mm, "end": v(17.54, 13.35) * mm});
            skLineSegment(sketch, "E333", {"start": v(17.54, 13.35) * mm, "end": v(17.6, 13.27) * mm});
            skLineSegment(sketch, "E334", {"start": v(17.6, 13.27) * mm, "end": v(17.66, 13.35) * mm});
            skLineSegment(sketch, "E335", {"start": v(17.66, 13.35) * mm, "end": v(18.02, 13.64) * mm});
            skLineSegment(sketch, "E336", {"start": v(18.02, 13.64) * mm, "end": v(18.41, 13.77) * mm});
            skLineSegment(sketch, "E337", {"start": v(18.41, 13.77) * mm, "end": v(18.54, 13.77) * mm});
            skLineSegment(sketch, "E338", {"start": v(18.54, 13.77) * mm, "end": v(21.13, 13.77) * mm});
            skLineSegment(sketch, "E339", {"start": v(21.13, 13.77) * mm, "end": v(21.16, 13.77) * mm});
            skLineSegment(sketch, "E340", {"start": v(21.16, 13.77) * mm, "end": v(21.25, 13.7) * mm});
            skLineSegment(sketch, "E341", {"start": v(21.25, 13.7) * mm, "end": v(21.3, 13.58) * mm});
            skLineSegment(sketch, "E342", {"start": v(21.3, 13.58) * mm, "end": v(21.3, 13.54) * mm});
            skLineSegment(sketch, "E343", {"start": v(21.3, 13.54) * mm, "end": v(21.3, 13.1) * mm});
            skLineSegment(sketch, "E344", {"start": v(21.3, 13.1) * mm, "end": v(21.3, 13.06) * mm});
            skLineSegment(sketch, "E345", {"start": v(21.3, 13.06) * mm, "end": v(21.25, 12.93) * mm});
            skLineSegment(sketch, "E346", {"start": v(21.25, 12.93) * mm, "end": v(21.16, 12.87) * mm});
            skLineSegment(sketch, "E347", {"start": v(21.16, 12.87) * mm, "end": v(21.13, 12.87) * mm});
            skLineSegment(sketch, "E348", {"start": v(21.13, 12.87) * mm, "end": v(18.54, 12.87) * mm});
            skLineSegment(sketch, "E349", {"start": v(18.54, 12.87) * mm, "end": v(18.44, 12.87) * mm});
            skLineSegment(sketch, "E350", {"start": v(18.44, 12.87) * mm, "end": v(18.13, 12.66) * mm});
            skLineSegment(sketch, "E351", {"start": v(18.13, 12.66) * mm, "end": v(17.97, 12.28) * mm});
            skLineSegment(sketch, "E352", {"start": v(17.97, 12.28) * mm, "end": v(17.97, 12.16) * mm});
            skLineSegment(sketch, "E353", {"start": v(17.97, 12.16) * mm, "end": v(17.97, 11.45) * mm});
            skLineSegment(sketch, "E354", {"start": v(17.97, 11.45) * mm, "end": v(21.13, 11.45) * mm});
            skLineSegment(sketch, "E355", {"start": v(21.13, 11.45) * mm, "end": v(21.16, 11.45) * mm});
            skLineSegment(sketch, "E356", {"start": v(21.16, 11.45) * mm, "end": v(21.25, 11.38) * mm});
            skLineSegment(sketch, "E357", {"start": v(21.25, 11.38) * mm, "end": v(21.3, 11.26) * mm});
            skLineSegment(sketch, "E358", {"start": v(21.3, 11.26) * mm, "end": v(21.3, 11.22) * mm});
            skLineSegment(sketch, "E359", {"start": v(21.3, 11.22) * mm, "end": v(21.3, 10.78) * mm});
            skLineSegment(sketch, "E360", {"start": v(21.3, 10.78) * mm, "end": v(21.3, 10.74) * mm});
            skLineSegment(sketch, "E361", {"start": v(21.3, 10.74) * mm, "end": v(21.25, 10.61) * mm});
            skLineSegment(sketch, "E362", {"start": v(21.25, 10.61) * mm, "end": v(21.16, 10.55) * mm});
            skLineSegment(sketch, "E363", {"start": v(21.16, 10.55) * mm, "end": v(21.13, 10.55) * mm});
            skLineSegment(sketch, "E364", {"start": v(21.13, 10.55) * mm, "end": v(14.26, 10.55) * mm});
            skLineSegment(sketch, "E365", {"start": v(14.26, 10.55) * mm, "end": v(14.2, 10.55) * mm});
            skLineSegment(sketch, "E366", {"start": v(14.2, 10.55) * mm, "end": v(14, 10.67) * mm});
            skLineSegment(sketch, "E367", {"start": v(14, 10.67) * mm, "end": v(13.9, 10.91) * mm});
            skLineSegment(sketch, "E368", {"start": v(13.9, 10.91) * mm, "end": v(13.9, 10.99) * mm});
            skLineSegment(sketch, "E369", {"start": v(13.9, 10.99) * mm, "end": v(13.9, 12.16) * mm});
            skLineSegment(sketch, "E370", {"start": v(13.9, 12.16) * mm, "end": v(13.9, 12.32) * mm});
            skLineSegment(sketch, "E371", {"start": v(13.9, 12.32) * mm, "end": v(14, 12.8) * mm});
            skLineSegment(sketch, "E372", {"start": v(14, 12.8) * mm, "end": v(14.27, 13.3) * mm});
            skLineSegment(sketch, "E373", {"start": v(14.27, 13.3) * mm, "end": v(14.68, 13.65) * mm});
            skLineSegment(sketch, "E374", {"start": v(14.68, 13.65) * mm, "end": v(15.06, 13.77) * mm});
            skLineSegment(sketch, "E375", {"start": v(15.06, 13.77) * mm, "end": v(15.18, 13.77) * mm});
            skLineSegment(sketch, "E376", {"start": v(15.18, 13.77) * mm, "end": v(16.68, 13.77) * mm});
            skLineSegment(sketch, "E377", {"start": v(15.2, 12.87) * mm, "end": v(15.1, 12.87) * mm});
            skLineSegment(sketch, "E378", {"start": v(15.1, 12.87) * mm, "end": v(14.8, 12.66) * mm});
            skLineSegment(sketch, "E379", {"start": v(14.8, 12.66) * mm, "end": v(14.63, 12.28) * mm});
            skLineSegment(sketch, "E380", {"start": v(14.63, 12.28) * mm, "end": v(14.63, 12.16) * mm});
            skLineSegment(sketch, "E381", {"start": v(14.63, 12.16) * mm, "end": v(14.63, 11.45) * mm});
            skLineSegment(sketch, "E382", {"start": v(14.63, 11.45) * mm, "end": v(17.26, 11.45) * mm});
            skLineSegment(sketch, "E383", {"start": v(17.26, 11.45) * mm, "end": v(17.26, 12.16) * mm});
            skLineSegment(sketch, "E384", {"start": v(17.26, 12.16) * mm, "end": v(17.26, 12.28) * mm});
            skLineSegment(sketch, "E385", {"start": v(17.26, 12.28) * mm, "end": v(17.09, 12.66) * mm});
            skLineSegment(sketch, "E386", {"start": v(17.09, 12.66) * mm, "end": v(16.78, 12.87) * mm});
            skLineSegment(sketch, "E387", {"start": v(16.78, 12.87) * mm, "end": v(16.68, 12.87) * mm});
            skLineSegment(sketch, "E388", {"start": v(16.68, 12.87) * mm, "end": v(15.2, 12.87) * mm});
            skLineSegment(sketch, "E389", {"start": v(15.57, 17.26) * mm, "end": v(15.18, 17.26) * mm});
            skLineSegment(sketch, "E390", {"start": v(15.18, 17.26) * mm, "end": v(15.08, 17.26) * mm});
            skLineSegment(sketch, "E391", {"start": v(15.08, 17.26) * mm, "end": v(14.78, 17.05) * mm});
            skLineSegment(sketch, "E392", {"start": v(14.78, 17.05) * mm, "end": v(14.6, 16.68) * mm});
            skLineSegment(sketch, "E393", {"start": v(14.6, 16.68) * mm, "end": v(14.6, 16.55) * mm});
            skLineSegment(sketch, "E394", {"start": v(14.6, 16.55) * mm, "end": v(14.6, 16.43) * mm});
            skLineSegment(sketch, "E395", {"start": v(14.6, 16.43) * mm, "end": v(14.77, 16.06) * mm});
            skLineSegment(sketch, "E396", {"start": v(14.77, 16.06) * mm, "end": v(15.08, 15.84) * mm});
            skLineSegment(sketch, "E397", {"start": v(15.08, 15.84) * mm, "end": v(15.18, 15.84) * mm});
            skLineSegment(sketch, "E398", {"start": v(15.18, 15.84) * mm, "end": v(20.02, 15.84) * mm});
            skLineSegment(sketch, "E399", {"start": v(20.02, 15.84) * mm, "end": v(20.12, 15.84) * mm});
            skLineSegment(sketch, "E400", {"start": v(20.12, 15.84) * mm, "end": v(20.42, 16.06) * mm});
            skLineSegment(sketch, "E401", {"start": v(20.42, 16.06) * mm, "end": v(20.6, 16.43) * mm});
            skLineSegment(sketch, "E402", {"start": v(20.6, 16.43) * mm, "end": v(20.6, 16.55) * mm});
            skLineSegment(sketch, "E403", {"start": v(20.6, 16.55) * mm, "end": v(20.6, 16.68) * mm});
            skLineSegment(sketch, "E404", {"start": v(20.6, 16.68) * mm, "end": v(20.43, 17.05) * mm});
            skLineSegment(sketch, "E405", {"start": v(20.43, 17.05) * mm, "end": v(20.12, 17.26) * mm});
            skLineSegment(sketch, "E406", {"start": v(20.12, 17.26) * mm, "end": v(20.02, 17.26) * mm});
            skLineSegment(sketch, "E407", {"start": v(20.02, 17.26) * mm, "end": v(17.95, 17.26) * mm});
            skLineSegment(sketch, "E408", {"start": v(17.95, 17.26) * mm, "end": v(17.95, 16.77) * mm});
            skLineSegment(sketch, "E409", {"start": v(17.95, 16.77) * mm, "end": v(17.95, 16.72) * mm});
            skLineSegment(sketch, "E410", {"start": v(17.95, 16.72) * mm, "end": v(17.9, 16.6) * mm});
            skLineSegment(sketch, "E411", {"start": v(17.9, 16.6) * mm, "end": v(17.8, 16.54) * mm});
            skLineSegment(sketch, "E412", {"start": v(17.8, 16.54) * mm, "end": v(17.77, 16.54) * mm});
            skLineSegment(sketch, "E413", {"start": v(17.77, 16.54) * mm, "end": v(17.4, 16.54) * mm});
            skLineSegment(sketch, "E414", {"start": v(17.4, 16.54) * mm, "end": v(17.38, 16.54) * mm});
            skLineSegment(sketch, "E415", {"start": v(17.38, 16.54) * mm, "end": v(17.29, 16.6) * mm});
            skLineSegment(sketch, "E416", {"start": v(17.29, 16.6) * mm, "end": v(17.24, 16.72) * mm});
            skLineSegment(sketch, "E417", {"start": v(17.24, 16.72) * mm, "end": v(17.24, 16.77) * mm});
            skLineSegment(sketch, "E418", {"start": v(17.24, 16.77) * mm, "end": v(17.24, 17.94) * mm});
            skLineSegment(sketch, "E419", {"start": v(17.24, 17.94) * mm, "end": v(17.24, 17.98) * mm});
            skLineSegment(sketch, "E420", {"start": v(17.24, 17.98) * mm, "end": v(17.29, 18.1) * mm});
            skLineSegment(sketch, "E421", {"start": v(17.29, 18.1) * mm, "end": v(17.38, 18.17) * mm});
            skLineSegment(sketch, "E422", {"start": v(17.38, 18.17) * mm, "end": v(17.4, 18.17) * mm});
            skLineSegment(sketch, "E423", {"start": v(17.4, 18.17) * mm, "end": v(20.02, 18.17) * mm});
            skLineSegment(sketch, "E424", {"start": v(20.02, 18.17) * mm, "end": v(20.14, 18.17) * mm});
            skLineSegment(sketch, "E425", {"start": v(20.14, 18.17) * mm, "end": v(20.52, 18.04) * mm});
            skLineSegment(sketch, "E426", {"start": v(20.52, 18.04) * mm, "end": v(20.93, 17.7) * mm});
            skLineSegment(sketch, "E427", {"start": v(20.93, 17.7) * mm, "end": v(21.2, 17.18) * mm});
            skLineSegment(sketch, "E428", {"start": v(21.2, 17.18) * mm, "end": v(21.3, 16.71) * mm});
            skLineSegment(sketch, "E429", {"start": v(21.3, 16.71) * mm, "end": v(21.3, 16.55) * mm});
            skLineSegment(sketch, "E430", {"start": v(21.3, 16.55) * mm, "end": v(21.3, 16.4) * mm});
            skLineSegment(sketch, "E431", {"start": v(21.3, 16.4) * mm, "end": v(21.2, 15.93) * mm});
            skLineSegment(sketch, "E432", {"start": v(21.2, 15.93) * mm, "end": v(20.93, 15.42) * mm});
            skLineSegment(sketch, "E433", {"start": v(20.93, 15.42) * mm, "end": v(20.52, 15.07) * mm});
            skLineSegment(sketch, "E434", {"start": v(20.52, 15.07) * mm, "end": v(20.14, 14.94) * mm});
            skLineSegment(sketch, "E435", {"start": v(20.14, 14.94) * mm, "end": v(20.02, 14.94) * mm});
            skLineSegment(sketch, "E436", {"start": v(20.02, 14.94) * mm, "end": v(15.18, 14.94) * mm});
            skLineSegment(sketch, "E437", {"start": v(15.18, 14.94) * mm, "end": v(15.06, 14.94) * mm});
            skLineSegment(sketch, "E438", {"start": v(15.06, 14.94) * mm, "end": v(14.68, 15.07) * mm});
            skLineSegment(sketch, "E439", {"start": v(14.68, 15.07) * mm, "end": v(14.27, 15.42) * mm});
            skLineSegment(sketch, "E440", {"start": v(14.27, 15.42) * mm, "end": v(14, 15.93) * mm});
            skLineSegment(sketch, "E441", {"start": v(14, 15.93) * mm, "end": v(13.9, 16.4) * mm});
            skLineSegment(sketch, "E442", {"start": v(13.9, 16.4) * mm, "end": v(13.9, 16.55) * mm});
            skLineSegment(sketch, "E443", {"start": v(13.9, 16.55) * mm, "end": v(13.9, 16.71) * mm});
            skLineSegment(sketch, "E444", {"start": v(13.9, 16.71) * mm, "end": v(14, 17.18) * mm});
            skLineSegment(sketch, "E445", {"start": v(14, 17.18) * mm, "end": v(14.27, 17.7) * mm});
            skLineSegment(sketch, "E446", {"start": v(14.27, 17.7) * mm, "end": v(14.68, 18.04) * mm});
            skLineSegment(sketch, "E447", {"start": v(14.68, 18.04) * mm, "end": v(15.06, 18.17) * mm});
            skLineSegment(sketch, "E448", {"start": v(15.06, 18.17) * mm, "end": v(15.18, 18.17) * mm});
            skLineSegment(sketch, "E449", {"start": v(15.18, 18.17) * mm, "end": v(15.57, 18.17) * mm});
            skLineSegment(sketch, "E450", {"start": v(15.57, 18.17) * mm, "end": v(15.6, 18.17) * mm});
            skLineSegment(sketch, "E451", {"start": v(15.6, 18.17) * mm, "end": v(15.69, 18.1) * mm});
            skLineSegment(sketch, "E452", {"start": v(15.69, 18.1) * mm, "end": v(15.74, 17.98) * mm});
            skLineSegment(sketch, "E453", {"start": v(15.74, 17.98) * mm, "end": v(15.74, 17.94) * mm});
            skLineSegment(sketch, "E454", {"start": v(15.74, 17.94) * mm, "end": v(15.74, 17.5) * mm});
            skLineSegment(sketch, "E455", {"start": v(15.74, 17.5) * mm, "end": v(15.74, 17.45) * mm});
            skLineSegment(sketch, "E456", {"start": v(15.74, 17.45) * mm, "end": v(15.69, 17.33) * mm});
            skLineSegment(sketch, "E457", {"start": v(15.69, 17.33) * mm, "end": v(15.6, 17.26) * mm});
            skLineSegment(sketch, "E458", {"start": v(15.6, 17.26) * mm, "end": v(15.57, 17.26) * mm});
            skLineSegment(sketch, "E459.bottom", {"start": v(-31.28, 26.63) * mm, "end": v(31.28, 26.63) * mm});
            skLineSegment(sketch, "E459.top", {"start": v(-31.28, -26.63) * mm, "end": v(31.28, -26.63) * mm});
            skLineSegment(sketch, "E459.left", {"start": v(-31.28, 26.63) * mm, "end": v(-31.28, -26.63) * mm});
            skLineSegment(sketch, "E459.right", {"start": v(31.28, 26.63) * mm, "end": v(31.28, -26.63) * mm});
            skPoint(sketch, "E459.middle", {"position": v(0, 0) * mm});
            skSolve(sketch);
        }
        {
            var Q0;
            Q0=makeQuery(id+"F0.imprint","IMPRINT",FACE,{"disambiguationData":[TD([[makeQuery(id+"F0.imprint","IMPRINT",EDGE,{"derivedFrom":sQuery(id+"F0.wireOp",EDGE,"E0")}),1.0]])]});
            extrude(context, id + "F1", {"entities" : qUnion([Q0]), "depth" : 18 * mm, "offsetDistance" : 25 * mm});
        }
        {
            var Q0;
            Q0=makeQuery(id+"F0.imprint","IMPRINT",FACE,{"disambiguationData":[TD([[makeQuery(id+"F0.imprint","IMPRINT",EDGE,{"derivedFrom":sQuery(id+"F0.wireOp",EDGE,"E0")}),-1.0]])]});
            var Q1;
            Q1=makeQuery(id+"F0.imprint","IMPRINT",FACE,{"disambiguationData":[TD([[makeQuery(id+"F0.imprint","IMPRINT",EDGE,{"derivedFrom":sQuery(id+"F0.wireOp",EDGE,"E377")}),1.0]])]});
            var Q2;
            Q2=makeQuery(id+"F0.imprint","IMPRINT",FACE,{"disambiguationData":[TD([[makeQuery(id+"F0.imprint","IMPRINT",EDGE,{"derivedFrom":sQuery(id+"F0.wireOp",EDGE,"E261")}),1.0]])]});
            var Q3;
            Q3=makeQuery(id+"F0.imprint","IMPRINT",FACE,{"disambiguationData":[TD([[makeQuery(id+"F0.imprint","IMPRINT",EDGE,{"derivedFrom":sQuery(id+"F0.wireOp",EDGE,"E273")}),1.0]])]});
            var Q4;
            Q4=makeQuery(id+"F0.imprint","IMPRINT",FACE,{"disambiguationData":[TD([[makeQuery(id+"F0.imprint","IMPRINT",EDGE,{"derivedFrom":sQuery(id+"F0.wireOp",EDGE,"E145")}),1.0]])]});
            extrude(context, id + "F2", {"entities" : qUnion([Q0, Q1, Q2, Q3, Q4]), "operationType" : NewBodyOperationType.ADD, "depth" : 13 * mm, "offsetDistance" : 25 * mm});
        }
        {
            var Q0;
            Q0=makeQuery(id+"F0.imprint","IMPRINT",FACE,{"disambiguationData":[TD([[makeQuery(id+"F0.imprint","IMPRINT",EDGE,{"derivedFrom":sQuery(id+"F0.wireOp",EDGE,"E13")}),-1.0]])]});
            var Q1;
            Q1=makeQuery(id+"F0.imprint","IMPRINT",FACE,{"disambiguationData":[TD([[makeQuery(id+"F0.imprint","IMPRINT",EDGE,{"derivedFrom":sQuery(id+"F0.wireOp",EDGE,"E56")}),-1.0]])]});
            var Q2;
            Q2=makeQuery(id+"F0.imprint","IMPRINT",FACE,{"disambiguationData":[TD([[makeQuery(id+"F0.imprint","IMPRINT",EDGE,{"derivedFrom":sQuery(id+"F0.wireOp",EDGE,"E101")}),-1.0]])]});
            var Q3;
            Q3=makeQuery(id+"F0.imprint","IMPRINT",FACE,{"disambiguationData":[TD([[makeQuery(id+"F0.imprint","IMPRINT",EDGE,{"derivedFrom":sQuery(id+"F0.wireOp",EDGE,"E121")}),-1.0]])]});
            var Q4;
            Q4=makeQuery(id+"F0.imprint","IMPRINT",FACE,{"disambiguationData":[TD([[makeQuery(id+"F0.imprint","IMPRINT",EDGE,{"derivedFrom":sQuery(id+"F0.wireOp",EDGE,"E157")}),-1.0]])]});
            var Q5;
            Q5=makeQuery(id+"F0.imprint","IMPRINT",FACE,{"disambiguationData":[TD([[makeQuery(id+"F0.imprint","IMPRINT",EDGE,{"derivedFrom":sQuery(id+"F0.wireOp",EDGE,"E202")}),-1.0]])]});
            var Q6;
            Q6=makeQuery(id+"F0.imprint","IMPRINT",FACE,{"disambiguationData":[TD([[makeQuery(id+"F0.imprint","IMPRINT",EDGE,{"derivedFrom":sQuery(id+"F0.wireOp",EDGE,"E228")}),-1.0]])]});
            var Q7;
            Q7=makeQuery(id+"F0.imprint","IMPRINT",FACE,{"disambiguationData":[TD([[makeQuery(id+"F0.imprint","IMPRINT",EDGE,{"derivedFrom":sQuery(id+"F0.wireOp",EDGE,"E285")}),-1.0]])]});
            var Q8;
            Q8=makeQuery(id+"F0.imprint","IMPRINT",FACE,{"disambiguationData":[TD([[makeQuery(id+"F0.imprint","IMPRINT",EDGE,{"derivedFrom":sQuery(id+"F0.wireOp",EDGE,"E330")}),-1.0]])]});
            var Q9;
            Q9=makeQuery(id+"F0.imprint","IMPRINT",FACE,{"disambiguationData":[TD([[makeQuery(id+"F0.imprint","IMPRINT",EDGE,{"derivedFrom":sQuery(id+"F0.wireOp",EDGE,"E389")}),-1.0]])]});
            extrude(context, id + "F3", {"entities" : qUnion([Q0, Q1, Q2, Q3, Q4, Q5, Q6, Q7, Q8, Q9]), "operationType" : NewBodyOperationType.ADD, "depth" : 14 * mm, "offsetDistance" : 25 * mm});
        }
        {
            var Q0;
            Q0=makeQuery(id+"F3.opExtrude","CAP_FACE",FACE,{"disambiguationData":[OSD([sQuery(id+"F0.wireOp",EDGE,"E13"),sQuery(id+"F0.wireOp",EDGE,"E14"),sQuery(id+"F0.wireOp",EDGE,"E15"),sQuery(id+"F0.wireOp",EDGE,"E16"),sQuery(id+"F0.wireOp",EDGE,"E17"),sQuery(id+"F0.wireOp",EDGE,"E18"),sQuery(id+"F0.wireOp",EDGE,"E19"),sQuery(id+"F0.wireOp",EDGE,"E20"),sQuery(id+"F0.wireOp",EDGE,"E21"),sQuery(id+"F0.wireOp",EDGE,"E22"),sQuery(id+"F0.wireOp",EDGE,"E23"),sQuery(id+"F0.wireOp",EDGE,"E24"),sQuery(id+"F0.wireOp",EDGE,"E25"),sQuery(id+"F0.wireOp",EDGE,"E26"),sQuery(id+"F0.wireOp",EDGE,"E27"),sQuery(id+"F0.wireOp",EDGE,"E28"),sQuery(id+"F0.wireOp",EDGE,"E29"),sQuery(id+"F0.wireOp",EDGE,"E30"),sQuery(id+"F0.wireOp",EDGE,"E31"),sQuery(id+"F0.wireOp",EDGE,"E32"),sQuery(id+"F0.wireOp",EDGE,"E33"),sQuery(id+"F0.wireOp",EDGE,"E34"),sQuery(id+"F0.wireOp",EDGE,"E35"),sQuery(id+"F0.wireOp",EDGE,"E36"),sQuery(id+"F0.wireOp",EDGE,"E37"),sQuery(id+"F0.wireOp",EDGE,"E38"),sQuery(id+"F0.wireOp",EDGE,"E39"),sQuery(id+"F0.wireOp",EDGE,"E40"),sQuery(id+"F0.wireOp",EDGE,"E41"),sQuery(id+"F0.wireOp",EDGE,"E42"),sQuery(id+"F0.wireOp",EDGE,"E43"),sQuery(id+"F0.wireOp",EDGE,"E44"),sQuery(id+"F0.wireOp",EDGE,"E45"),sQuery(id+"F0.wireOp",EDGE,"E46"),sQuery(id+"F0.wireOp",EDGE,"E47"),sQuery(id+"F0.wireOp",EDGE,"E48"),sQuery(id+"F0.wireOp",EDGE,"E49"),sQuery(id+"F0.wireOp",EDGE,"E50"),sQuery(id+"F0.wireOp",EDGE,"E51"),sQuery(id+"F0.wireOp",EDGE,"E52"),sQuery(id+"F0.wireOp",EDGE,"E53"),sQuery(id+"F0.wireOp",EDGE,"E54"),sQuery(id+"F0.wireOp",EDGE,"E55")])],"isStart":false});
            var Q1;
            Q1=makeQuery(id+"F3.opExtrude","CAP_FACE",FACE,{"disambiguationData":[OSD([sQuery(id+"F0.wireOp",EDGE,"E56"),sQuery(id+"F0.wireOp",EDGE,"E57"),sQuery(id+"F0.wireOp",EDGE,"E58"),sQuery(id+"F0.wireOp",EDGE,"E59"),sQuery(id+"F0.wireOp",EDGE,"E60"),sQuery(id+"F0.wireOp",EDGE,"E61"),sQuery(id+"F0.wireOp",EDGE,"E62"),sQuery(id+"F0.wireOp",EDGE,"E63"),sQuery(id+"F0.wireOp",EDGE,"E64"),sQuery(id+"F0.wireOp",EDGE,"E65"),sQuery(id+"F0.wireOp",EDGE,"E66"),sQuery(id+"F0.wireOp",EDGE,"E67"),sQuery(id+"F0.wireOp",EDGE,"E68"),sQuery(id+"F0.wireOp",EDGE,"E69"),sQuery(id+"F0.wireOp",EDGE,"E70"),sQuery(id+"F0.wireOp",EDGE,"E71"),sQuery(id+"F0.wireOp",EDGE,"E72"),sQuery(id+"F0.wireOp",EDGE,"E73"),sQuery(id+"F0.wireOp",EDGE,"E74"),sQuery(id+"F0.wireOp",EDGE,"E75"),sQuery(id+"F0.wireOp",EDGE,"E76"),sQuery(id+"F0.wireOp",EDGE,"E77"),sQuery(id+"F0.wireOp",EDGE,"E78"),sQuery(id+"F0.wireOp",EDGE,"E79"),sQuery(id+"F0.wireOp",EDGE,"E80"),sQuery(id+"F0.wireOp",EDGE,"E81"),sQuery(id+"F0.wireOp",EDGE,"E82"),sQuery(id+"F0.wireOp",EDGE,"E83"),sQuery(id+"F0.wireOp",EDGE,"E84"),sQuery(id+"F0.wireOp",EDGE,"E85"),sQuery(id+"F0.wireOp",EDGE,"E86"),sQuery(id+"F0.wireOp",EDGE,"E87"),sQuery(id+"F0.wireOp",EDGE,"E88"),sQuery(id+"F0.wireOp",EDGE,"E89"),sQuery(id+"F0.wireOp",EDGE,"E90"),sQuery(id+"F0.wireOp",EDGE,"E91"),sQuery(id+"F0.wireOp",EDGE,"E92"),sQuery(id+"F0.wireOp",EDGE,"E93"),sQuery(id+"F0.wireOp",EDGE,"E94"),sQuery(id+"F0.wireOp",EDGE,"E95"),sQuery(id+"F0.wireOp",EDGE,"E96"),sQuery(id+"F0.wireOp",EDGE,"E97"),sQuery(id+"F0.wireOp",EDGE,"E98"),sQuery(id+"F0.wireOp",EDGE,"E99"),sQuery(id+"F0.wireOp",EDGE,"E100")])],"isStart":false});
            var Q2;
            Q2=makeQuery(id+"F3.opExtrude","CAP_FACE",FACE,{"disambiguationData":[OSD([sQuery(id+"F0.wireOp",EDGE,"E101"),sQuery(id+"F0.wireOp",EDGE,"E102"),sQuery(id+"F0.wireOp",EDGE,"E103"),sQuery(id+"F0.wireOp",EDGE,"E104"),sQuery(id+"F0.wireOp",EDGE,"E105"),sQuery(id+"F0.wireOp",EDGE,"E106"),sQuery(id+"F0.wireOp",EDGE,"E107"),sQuery(id+"F0.wireOp",EDGE,"E108"),sQuery(id+"F0.wireOp",EDGE,"E109"),sQuery(id+"F0.wireOp",EDGE,"E110"),sQuery(id+"F0.wireOp",EDGE,"E111"),sQuery(id+"F0.wireOp",EDGE,"E112"),sQuery(id+"F0.wireOp",EDGE,"E113"),sQuery(id+"F0.wireOp",EDGE,"E114"),sQuery(id+"F0.wireOp",EDGE,"E115"),sQuery(id+"F0.wireOp",EDGE,"E116"),sQuery(id+"F0.wireOp",EDGE,"E117"),sQuery(id+"F0.wireOp",EDGE,"E118"),sQuery(id+"F0.wireOp",EDGE,"E119"),sQuery(id+"F0.wireOp",EDGE,"E120")])],"isStart":false});
            var Q3;
            Q3=makeQuery(id+"F3.opExtrude","CAP_FACE",FACE,{"disambiguationData":[OSD([sQuery(id+"F0.wireOp",EDGE,"E121"),sQuery(id+"F0.wireOp",EDGE,"E122"),sQuery(id+"F0.wireOp",EDGE,"E123"),sQuery(id+"F0.wireOp",EDGE,"E124"),sQuery(id+"F0.wireOp",EDGE,"E125"),sQuery(id+"F0.wireOp",EDGE,"E126"),sQuery(id+"F0.wireOp",EDGE,"E127"),sQuery(id+"F0.wireOp",EDGE,"E128"),sQuery(id+"F0.wireOp",EDGE,"E129"),sQuery(id+"F0.wireOp",EDGE,"E130"),sQuery(id+"F0.wireOp",EDGE,"E131"),sQuery(id+"F0.wireOp",EDGE,"E132"),sQuery(id+"F0.wireOp",EDGE,"E133"),sQuery(id+"F0.wireOp",EDGE,"E134"),sQuery(id+"F0.wireOp",EDGE,"E135"),sQuery(id+"F0.wireOp",EDGE,"E136"),sQuery(id+"F0.wireOp",EDGE,"E137"),sQuery(id+"F0.wireOp",EDGE,"E138"),sQuery(id+"F0.wireOp",EDGE,"E139"),sQuery(id+"F0.wireOp",EDGE,"E140"),sQuery(id+"F0.wireOp",EDGE,"E141"),sQuery(id+"F0.wireOp",EDGE,"E142"),sQuery(id+"F0.wireOp",EDGE,"E143"),sQuery(id+"F0.wireOp",EDGE,"E144"),sQuery(id+"F0.wireOp",EDGE,"E145"),sQuery(id+"F0.wireOp",EDGE,"E146"),sQuery(id+"F0.wireOp",EDGE,"E147"),sQuery(id+"F0.wireOp",EDGE,"E148"),sQuery(id+"F0.wireOp",EDGE,"E149"),sQuery(id+"F0.wireOp",EDGE,"E150"),sQuery(id+"F0.wireOp",EDGE,"E151"),sQuery(id+"F0.wireOp",EDGE,"E152"),sQuery(id+"F0.wireOp",EDGE,"E153"),sQuery(id+"F0.wireOp",EDGE,"E154"),sQuery(id+"F0.wireOp",EDGE,"E155"),sQuery(id+"F0.wireOp",EDGE,"E156")])],"isStart":false});
            var Q4;
            Q4=makeQuery(id+"F3.opExtrude","CAP_FACE",FACE,{"disambiguationData":[OSD([sQuery(id+"F0.wireOp",EDGE,"E157"),sQuery(id+"F0.wireOp",EDGE,"E158"),sQuery(id+"F0.wireOp",EDGE,"E159"),sQuery(id+"F0.wireOp",EDGE,"E160"),sQuery(id+"F0.wireOp",EDGE,"E161"),sQuery(id+"F0.wireOp",EDGE,"E162"),sQuery(id+"F0.wireOp",EDGE,"E163"),sQuery(id+"F0.wireOp",EDGE,"E164"),sQuery(id+"F0.wireOp",EDGE,"E165"),sQuery(id+"F0.wireOp",EDGE,"E166"),sQuery(id+"F0.wireOp",EDGE,"E167"),sQuery(id+"F0.wireOp",EDGE,"E168"),sQuery(id+"F0.wireOp",EDGE,"E169"),sQuery(id+"F0.wireOp",EDGE,"E170"),sQuery(id+"F0.wireOp",EDGE,"E171"),sQuery(id+"F0.wireOp",EDGE,"E172"),sQuery(id+"F0.wireOp",EDGE,"E173"),sQuery(id+"F0.wireOp",EDGE,"E174"),sQuery(id+"F0.wireOp",EDGE,"E175"),sQuery(id+"F0.wireOp",EDGE,"E176"),sQuery(id+"F0.wireOp",EDGE,"E177"),sQuery(id+"F0.wireOp",EDGE,"E178"),sQuery(id+"F0.wireOp",EDGE,"E179"),sQuery(id+"F0.wireOp",EDGE,"E180"),sQuery(id+"F0.wireOp",EDGE,"E181"),sQuery(id+"F0.wireOp",EDGE,"E182"),sQuery(id+"F0.wireOp",EDGE,"E183"),sQuery(id+"F0.wireOp",EDGE,"E184"),sQuery(id+"F0.wireOp",EDGE,"E185"),sQuery(id+"F0.wireOp",EDGE,"E186"),sQuery(id+"F0.wireOp",EDGE,"E187"),sQuery(id+"F0.wireOp",EDGE,"E188"),sQuery(id+"F0.wireOp",EDGE,"E189"),sQuery(id+"F0.wireOp",EDGE,"E190"),sQuery(id+"F0.wireOp",EDGE,"E191"),sQuery(id+"F0.wireOp",EDGE,"E192"),sQuery(id+"F0.wireOp",EDGE,"E193"),sQuery(id+"F0.wireOp",EDGE,"E194"),sQuery(id+"F0.wireOp",EDGE,"E195"),sQuery(id+"F0.wireOp",EDGE,"E196"),sQuery(id+"F0.wireOp",EDGE,"E197"),sQuery(id+"F0.wireOp",EDGE,"E198"),sQuery(id+"F0.wireOp",EDGE,"E199"),sQuery(id+"F0.wireOp",EDGE,"E200"),sQuery(id+"F0.wireOp",EDGE,"E201")])],"isStart":false});
            var Q5;
            Q5=makeQuery(id+"F3.opExtrude","CAP_FACE",FACE,{"disambiguationData":[OSD([sQuery(id+"F0.wireOp",EDGE,"E228"),sQuery(id+"F0.wireOp",EDGE,"E229"),sQuery(id+"F0.wireOp",EDGE,"E230"),sQuery(id+"F0.wireOp",EDGE,"E231"),sQuery(id+"F0.wireOp",EDGE,"E232"),sQuery(id+"F0.wireOp",EDGE,"E233"),sQuery(id+"F0.wireOp",EDGE,"E234"),sQuery(id+"F0.wireOp",EDGE,"E235"),sQuery(id+"F0.wireOp",EDGE,"E236"),sQuery(id+"F0.wireOp",EDGE,"E237"),sQuery(id+"F0.wireOp",EDGE,"E238"),sQuery(id+"F0.wireOp",EDGE,"E239"),sQuery(id+"F0.wireOp",EDGE,"E240"),sQuery(id+"F0.wireOp",EDGE,"E241"),sQuery(id+"F0.wireOp",EDGE,"E242"),sQuery(id+"F0.wireOp",EDGE,"E243"),sQuery(id+"F0.wireOp",EDGE,"E244"),sQuery(id+"F0.wireOp",EDGE,"E245"),sQuery(id+"F0.wireOp",EDGE,"E246"),sQuery(id+"F0.wireOp",EDGE,"E247"),sQuery(id+"F0.wireOp",EDGE,"E248"),sQuery(id+"F0.wireOp",EDGE,"E249"),sQuery(id+"F0.wireOp",EDGE,"E250"),sQuery(id+"F0.wireOp",EDGE,"E251"),sQuery(id+"F0.wireOp",EDGE,"E252"),sQuery(id+"F0.wireOp",EDGE,"E253"),sQuery(id+"F0.wireOp",EDGE,"E254"),sQuery(id+"F0.wireOp",EDGE,"E255"),sQuery(id+"F0.wireOp",EDGE,"E256"),sQuery(id+"F0.wireOp",EDGE,"E257"),sQuery(id+"F0.wireOp",EDGE,"E258"),sQuery(id+"F0.wireOp",EDGE,"E259"),sQuery(id+"F0.wireOp",EDGE,"E260"),sQuery(id+"F0.wireOp",EDGE,"E261"),sQuery(id+"F0.wireOp",EDGE,"E262"),sQuery(id+"F0.wireOp",EDGE,"E263"),sQuery(id+"F0.wireOp",EDGE,"E264"),sQuery(id+"F0.wireOp",EDGE,"E265"),sQuery(id+"F0.wireOp",EDGE,"E266"),sQuery(id+"F0.wireOp",EDGE,"E267"),sQuery(id+"F0.wireOp",EDGE,"E268"),sQuery(id+"F0.wireOp",EDGE,"E269"),sQuery(id+"F0.wireOp",EDGE,"E270"),sQuery(id+"F0.wireOp",EDGE,"E271"),sQuery(id+"F0.wireOp",EDGE,"E272"),sQuery(id+"F0.wireOp",EDGE,"E273"),sQuery(id+"F0.wireOp",EDGE,"E274"),sQuery(id+"F0.wireOp",EDGE,"E275"),sQuery(id+"F0.wireOp",EDGE,"E276"),sQuery(id+"F0.wireOp",EDGE,"E277"),sQuery(id+"F0.wireOp",EDGE,"E278"),sQuery(id+"F0.wireOp",EDGE,"E279"),sQuery(id+"F0.wireOp",EDGE,"E280"),sQuery(id+"F0.wireOp",EDGE,"E281"),sQuery(id+"F0.wireOp",EDGE,"E282"),sQuery(id+"F0.wireOp",EDGE,"E283"),sQuery(id+"F0.wireOp",EDGE,"E284")])],"isStart":false});
            var Q6;
            Q6=makeQuery(id+"F3.opExtrude","CAP_FACE",FACE,{"disambiguationData":[OSD([sQuery(id+"F0.wireOp",EDGE,"E202"),sQuery(id+"F0.wireOp",EDGE,"E203"),sQuery(id+"F0.wireOp",EDGE,"E204"),sQuery(id+"F0.wireOp",EDGE,"E205"),sQuery(id+"F0.wireOp",EDGE,"E206"),sQuery(id+"F0.wireOp",EDGE,"E207"),sQuery(id+"F0.wireOp",EDGE,"E208"),sQuery(id+"F0.wireOp",EDGE,"E209"),sQuery(id+"F0.wireOp",EDGE,"E210"),sQuery(id+"F0.wireOp",EDGE,"E211"),sQuery(id+"F0.wireOp",EDGE,"E212"),sQuery(id+"F0.wireOp",EDGE,"E213"),sQuery(id+"F0.wireOp",EDGE,"E214"),sQuery(id+"F0.wireOp",EDGE,"E215"),sQuery(id+"F0.wireOp",EDGE,"E216"),sQuery(id+"F0.wireOp",EDGE,"E217"),sQuery(id+"F0.wireOp",EDGE,"E218"),sQuery(id+"F0.wireOp",EDGE,"E219"),sQuery(id+"F0.wireOp",EDGE,"E220"),sQuery(id+"F0.wireOp",EDGE,"E221"),sQuery(id+"F0.wireOp",EDGE,"E222"),sQuery(id+"F0.wireOp",EDGE,"E223"),sQuery(id+"F0.wireOp",EDGE,"E224"),sQuery(id+"F0.wireOp",EDGE,"E225"),sQuery(id+"F0.wireOp",EDGE,"E226"),sQuery(id+"F0.wireOp",EDGE,"E227")])],"isStart":false});
            var Q7;
            Q7=makeQuery(id+"F3.opExtrude","CAP_FACE",FACE,{"disambiguationData":[OSD([sQuery(id+"F0.wireOp",EDGE,"E285"),sQuery(id+"F0.wireOp",EDGE,"E286"),sQuery(id+"F0.wireOp",EDGE,"E287"),sQuery(id+"F0.wireOp",EDGE,"E288"),sQuery(id+"F0.wireOp",EDGE,"E289"),sQuery(id+"F0.wireOp",EDGE,"E290"),sQuery(id+"F0.wireOp",EDGE,"E291"),sQuery(id+"F0.wireOp",EDGE,"E292"),sQuery(id+"F0.wireOp",EDGE,"E293"),sQuery(id+"F0.wireOp",EDGE,"E294"),sQuery(id+"F0.wireOp",EDGE,"E295"),sQuery(id+"F0.wireOp",EDGE,"E296"),sQuery(id+"F0.wireOp",EDGE,"E297"),sQuery(id+"F0.wireOp",EDGE,"E298"),sQuery(id+"F0.wireOp",EDGE,"E299"),sQuery(id+"F0.wireOp",EDGE,"E300"),sQuery(id+"F0.wireOp",EDGE,"E301"),sQuery(id+"F0.wireOp",EDGE,"E302"),sQuery(id+"F0.wireOp",EDGE,"E303"),sQuery(id+"F0.wireOp",EDGE,"E304"),sQuery(id+"F0.wireOp",EDGE,"E305"),sQuery(id+"F0.wireOp",EDGE,"E306"),sQuery(id+"F0.wireOp",EDGE,"E307"),sQuery(id+"F0.wireOp",EDGE,"E308"),sQuery(id+"F0.wireOp",EDGE,"E309"),sQuery(id+"F0.wireOp",EDGE,"E310"),sQuery(id+"F0.wireOp",EDGE,"E311"),sQuery(id+"F0.wireOp",EDGE,"E312"),sQuery(id+"F0.wireOp",EDGE,"E313"),sQuery(id+"F0.wireOp",EDGE,"E314"),sQuery(id+"F0.wireOp",EDGE,"E315"),sQuery(id+"F0.wireOp",EDGE,"E316"),sQuery(id+"F0.wireOp",EDGE,"E317"),sQuery(id+"F0.wireOp",EDGE,"E318"),sQuery(id+"F0.wireOp",EDGE,"E319"),sQuery(id+"F0.wireOp",EDGE,"E320"),sQuery(id+"F0.wireOp",EDGE,"E321"),sQuery(id+"F0.wireOp",EDGE,"E322"),sQuery(id+"F0.wireOp",EDGE,"E323"),sQuery(id+"F0.wireOp",EDGE,"E324"),sQuery(id+"F0.wireOp",EDGE,"E325"),sQuery(id+"F0.wireOp",EDGE,"E326"),sQuery(id+"F0.wireOp",EDGE,"E327"),sQuery(id+"F0.wireOp",EDGE,"E328"),sQuery(id+"F0.wireOp",EDGE,"E329")])],"isStart":false});
            var Q8;
            Q8=makeQuery(id+"F3.opExtrude","CAP_FACE",FACE,{"disambiguationData":[OSD([sQuery(id+"F0.wireOp",EDGE,"E330"),sQuery(id+"F0.wireOp",EDGE,"E331"),sQuery(id+"F0.wireOp",EDGE,"E332"),sQuery(id+"F0.wireOp",EDGE,"E333"),sQuery(id+"F0.wireOp",EDGE,"E334"),sQuery(id+"F0.wireOp",EDGE,"E335"),sQuery(id+"F0.wireOp",EDGE,"E336"),sQuery(id+"F0.wireOp",EDGE,"E337"),sQuery(id+"F0.wireOp",EDGE,"E338"),sQuery(id+"F0.wireOp",EDGE,"E339"),sQuery(id+"F0.wireOp",EDGE,"E340"),sQuery(id+"F0.wireOp",EDGE,"E341"),sQuery(id+"F0.wireOp",EDGE,"E342"),sQuery(id+"F0.wireOp",EDGE,"E343"),sQuery(id+"F0.wireOp",EDGE,"E344"),sQuery(id+"F0.wireOp",EDGE,"E345"),sQuery(id+"F0.wireOp",EDGE,"E346"),sQuery(id+"F0.wireOp",EDGE,"E347"),sQuery(id+"F0.wireOp",EDGE,"E348"),sQuery(id+"F0.wireOp",EDGE,"E349"),sQuery(id+"F0.wireOp",EDGE,"E350"),sQuery(id+"F0.wireOp",EDGE,"E351"),sQuery(id+"F0.wireOp",EDGE,"E352"),sQuery(id+"F0.wireOp",EDGE,"E353"),sQuery(id+"F0.wireOp",EDGE,"E354"),sQuery(id+"F0.wireOp",EDGE,"E355"),sQuery(id+"F0.wireOp",EDGE,"E356"),sQuery(id+"F0.wireOp",EDGE,"E357"),sQuery(id+"F0.wireOp",EDGE,"E358"),sQuery(id+"F0.wireOp",EDGE,"E359"),sQuery(id+"F0.wireOp",EDGE,"E360"),sQuery(id+"F0.wireOp",EDGE,"E361"),sQuery(id+"F0.wireOp",EDGE,"E362"),sQuery(id+"F0.wireOp",EDGE,"E363"),sQuery(id+"F0.wireOp",EDGE,"E364"),sQuery(id+"F0.wireOp",EDGE,"E365"),sQuery(id+"F0.wireOp",EDGE,"E366"),sQuery(id+"F0.wireOp",EDGE,"E367"),sQuery(id+"F0.wireOp",EDGE,"E368"),sQuery(id+"F0.wireOp",EDGE,"E369"),sQuery(id+"F0.wireOp",EDGE,"E370"),sQuery(id+"F0.wireOp",EDGE,"E371"),sQuery(id+"F0.wireOp",EDGE,"E372"),sQuery(id+"F0.wireOp",EDGE,"E373"),sQuery(id+"F0.wireOp",EDGE,"E374"),sQuery(id+"F0.wireOp",EDGE,"E375"),sQuery(id+"F0.wireOp",EDGE,"E376"),sQuery(id+"F0.wireOp",EDGE,"E377"),sQuery(id+"F0.wireOp",EDGE,"E378"),sQuery(id+"F0.wireOp",EDGE,"E379"),sQuery(id+"F0.wireOp",EDGE,"E380"),sQuery(id+"F0.wireOp",EDGE,"E381"),sQuery(id+"F0.wireOp",EDGE,"E382"),sQuery(id+"F0.wireOp",EDGE,"E383"),sQuery(id+"F0.wireOp",EDGE,"E384"),sQuery(id+"F0.wireOp",EDGE,"E385"),sQuery(id+"F0.wireOp",EDGE,"E386"),sQuery(id+"F0.wireOp",EDGE,"E387"),sQuery(id+"F0.wireOp",EDGE,"E388")])],"isStart":false});
            var Q9;
            Q9=makeQuery(id+"F3.opExtrude","CAP_FACE",FACE,{"disambiguationData":[OSD([sQuery(id+"F0.wireOp",EDGE,"E389"),sQuery(id+"F0.wireOp",EDGE,"E390"),sQuery(id+"F0.wireOp",EDGE,"E391"),sQuery(id+"F0.wireOp",EDGE,"E392"),sQuery(id+"F0.wireOp",EDGE,"E393"),sQuery(id+"F0.wireOp",EDGE,"E394"),sQuery(id+"F0.wireOp",EDGE,"E395"),sQuery(id+"F0.wireOp",EDGE,"E396"),sQuery(id+"F0.wireOp",EDGE,"E397"),sQuery(id+"F0.wireOp",EDGE,"E398"),sQuery(id+"F0.wireOp",EDGE,"E399"),sQuery(id+"F0.wireOp",EDGE,"E400"),sQuery(id+"F0.wireOp",EDGE,"E401"),sQuery(id+"F0.wireOp",EDGE,"E402"),sQuery(id+"F0.wireOp",EDGE,"E403"),sQuery(id+"F0.wireOp",EDGE,"E404"),sQuery(id+"F0.wireOp",EDGE,"E405"),sQuery(id+"F0.wireOp",EDGE,"E406"),sQuery(id+"F0.wireOp",EDGE,"E407"),sQuery(id+"F0.wireOp",EDGE,"E408"),sQuery(id+"F0.wireOp",EDGE,"E409"),sQuery(id+"F0.wireOp",EDGE,"E410"),sQuery(id+"F0.wireOp",EDGE,"E411"),sQuery(id+"F0.wireOp",EDGE,"E412"),sQuery(id+"F0.wireOp",EDGE,"E413"),sQuery(id+"F0.wireOp",EDGE,"E414"),sQuery(id+"F0.wireOp",EDGE,"E415"),sQuery(id+"F0.wireOp",EDGE,"E416"),sQuery(id+"F0.wireOp",EDGE,"E417"),sQuery(id+"F0.wireOp",EDGE,"E418"),sQuery(id+"F0.wireOp",EDGE,"E419"),sQuery(id+"F0.wireOp",EDGE,"E420"),sQuery(id+"F0.wireOp",EDGE,"E421"),sQuery(id+"F0.wireOp",EDGE,"E422"),sQuery(id+"F0.wireOp",EDGE,"E423"),sQuery(id+"F0.wireOp",EDGE,"E424"),sQuery(id+"F0.wireOp",EDGE,"E425"),sQuery(id+"F0.wireOp",EDGE,"E426"),sQuery(id+"F0.wireOp",EDGE,"E427"),sQuery(id+"F0.wireOp",EDGE,"E428"),sQuery(id+"F0.wireOp",EDGE,"E429"),sQuery(id+"F0.wireOp",EDGE,"E430"),sQuery(id+"F0.wireOp",EDGE,"E431"),sQuery(id+"F0.wireOp",EDGE,"E432"),sQuery(id+"F0.wireOp",EDGE,"E433"),sQuery(id+"F0.wireOp",EDGE,"E434"),sQuery(id+"F0.wireOp",EDGE,"E435"),sQuery(id+"F0.wireOp",EDGE,"E436"),sQuery(id+"F0.wireOp",EDGE,"E437"),sQuery(id+"F0.wireOp",EDGE,"E438"),sQuery(id+"F0.wireOp",EDGE,"E439"),sQuery(id+"F0.wireOp",EDGE,"E440"),sQuery(id+"F0.wireOp",EDGE,"E441"),sQuery(id+"F0.wireOp",EDGE,"E442"),sQuery(id+"F0.wireOp",EDGE,"E443"),sQuery(id+"F0.wireOp",EDGE,"E444"),sQuery(id+"F0.wireOp",EDGE,"E445"),sQuery(id+"F0.wireOp",EDGE,"E446"),sQuery(id+"F0.wireOp",EDGE,"E447"),sQuery(id+"F0.wireOp",EDGE,"E448"),sQuery(id+"F0.wireOp",EDGE,"E449"),sQuery(id+"F0.wireOp",EDGE,"E450"),sQuery(id+"F0.wireOp",EDGE,"E451"),sQuery(id+"F0.wireOp",EDGE,"E452"),sQuery(id+"F0.wireOp",EDGE,"E453"),sQuery(id+"F0.wireOp",EDGE,"E454"),sQuery(id+"F0.wireOp",EDGE,"E455"),sQuery(id+"F0.wireOp",EDGE,"E456"),sQuery(id+"F0.wireOp",EDGE,"E457"),sQuery(id+"F0.wireOp",EDGE,"E458")])],"isStart":false});
            fillet(context, id + "F4", {"entities" : qUnion([Q0, Q1, Q2, Q3, Q4, Q5, Q6, Q7, Q8, Q9]), "radius" : 0.34 * mm, "tangentPropagation" : true, "allowEdgeOverflow" : false});
        }
    });
